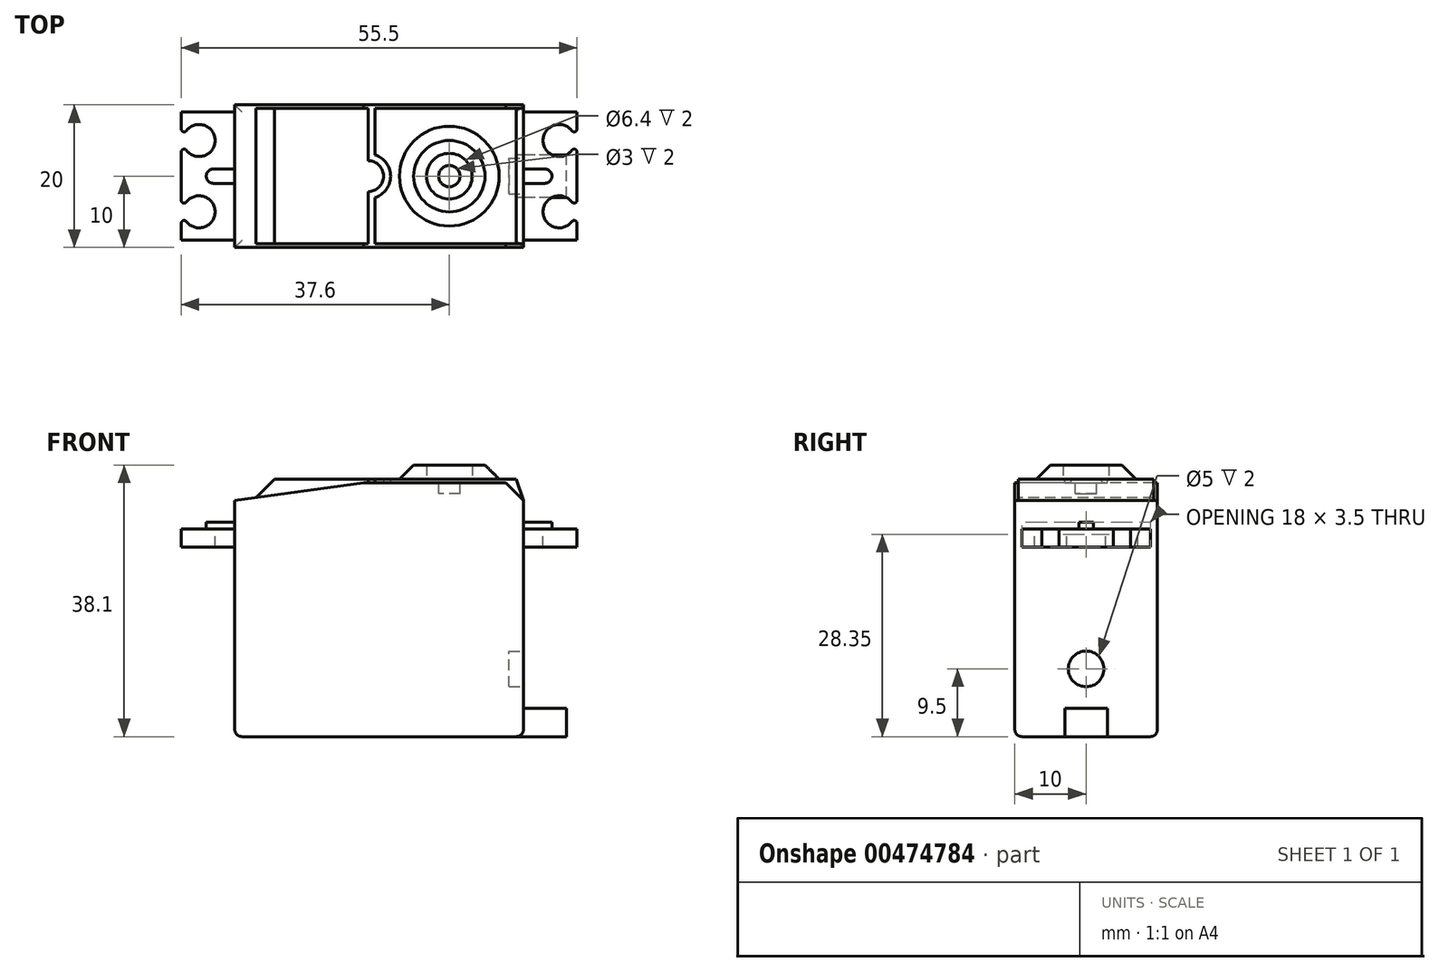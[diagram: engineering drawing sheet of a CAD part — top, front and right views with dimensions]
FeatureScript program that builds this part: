
annotation { "Feature Type Name" : "Feature", "Feature Type Description" : "" }
export const myFeature = defineFeature(function(context is Context, id is Id, definition is map)
    precondition{}
    {
        {
            var Q0;
            Q0=qCreatedBy(makeId("Front.planeOp"),FACE);
            var sketch = newSketch(context, id + "F0", { "sketchPlane" : qUnion([Q0])});
            skLineSegment(sketch, "E0.bottom", {"start": v(0, 0) * mm, "end": v(40.5, 0) * mm});
            skLineSegment(sketch, "E0.top", {"start": v(0, 36.1) * mm, "end": v(40.5, 36.1) * mm});
            skLineSegment(sketch, "E0.left", {"start": v(0, 0) * mm, "end": v(0, 26.6) * mm});
            skLineSegment(sketch, "E0.right", {"start": v(40.5, 0) * mm, "end": v(40.5, 26.6) * mm});
            skLineSegment(sketch, "E1", {"start": v(0, 29.1) * mm, "end": v(-7.5, 29.1) * mm});
            skLineSegment(sketch, "E2", {"start": v(-7.5, 29.1) * mm, "end": v(-7.5, 26.6) * mm});
            skLineSegment(sketch, "E3", {"start": v(-7.5, 26.6) * mm, "end": v(0, 26.6) * mm});
            skLineSegment(sketch, "E4", {"start": v(40.5, 29.1) * mm, "end": v(48, 29.1) * mm});
            skLineSegment(sketch, "E5", {"start": v(48, 29.1) * mm, "end": v(48, 26.6) * mm});
            skLineSegment(sketch, "E6", {"start": v(48, 26.6) * mm, "end": v(40.5, 26.6) * mm});
            skLineSegment(sketch, "E7.trimOffspring", {"start": v(0, 29.1) * mm, "end": v(0, 36.1) * mm});
            skLineSegment(sketch, "E8.trimOffspring", {"start": v(40.5, 29.1) * mm, "end": v(40.5, 36.1) * mm});
            skSolve(sketch);
        }
        {
            var Q0;
            Q0=qSketchRegion(id+"F0",true);
            extrude(context, id + "F1", {"entities" : qUnion([Q0]), "depth" : 20 * mm, "offsetDistance" : 25 * mm});
        }
        {
            var Q0;
            Q0=makeQuery(id+"F1.opExtrude","SWEPT_FACE",FACE,{"disambiguationData":[OSD([sQuery(id+"F0.wireOp",EDGE,"E1")])]});
            var sketch = newSketch(context, id + "F2", { "sketchPlane" : qUnion([Q0])});
            skLineSegment(sketch, "E9", {"start": v(0, -1) * mm, "end": v(-7.5, -1) * mm});
            skLineSegment(sketch, "E10", {"start": v(-7.5, -19) * mm, "end": v(0, -19) * mm});
            skLineSegment(sketch, "E11", {"start": v(0, -19) * mm, "end": v(0, -20) * mm});
            skLineSegment(sketch, "E12", {"start": v(0, -20) * mm, "end": v(-7.5, -20) * mm});
            skLineSegment(sketch, "E13", {"start": v(-7.5, 0) * mm, "end": v(0, 0) * mm});
            skArc(sketch, "E14", {"start": v(-6.8, -6.36) * mm, "mid": v(-2.75, -5) * mm, "end": v(-6.8, -3.64) * mm});
            skArc(sketch, "E15", {"start": v(-6.8, -16.36) * mm, "mid": v(-2.75, -15) * mm, "end": v(-6.8, -13.64) * mm});
            skLineSegment(sketch, "E16", {"start": v(-5, -5) * mm, "end": v(-5, -15) * mm, "construction": true});
            skLineSegment(sketch, "E17", {"start": v(-7.5, 0) * mm, "end": v(-7.5, -1) * mm});
            skLineSegment(sketch, "E18", {"start": v(-7.5, -19) * mm, "end": v(-7.5, -20) * mm});
            skLineSegment(sketch, "E19", {"start": v(20.25, 0) * mm, "end": v(20.25, -20) * mm, "construction": true});
            skArc(sketch, "E20", {"start": v(-7.5, -3.4) * mm, "mid": v(-7.23, -3.77) * mm, "end": v(-6.8, -3.64) * mm});
            skArc(sketch, "E21", {"start": v(-6.8, -6.36) * mm, "mid": v(-7.23, -6.23) * mm, "end": v(-7.5, -6.6) * mm});
            skLineSegment(sketch, "E22", {"start": v(-7.5, -5) * mm, "end": v(-5, -5) * mm, "construction": true});
            skLineSegment(sketch, "E23", {"start": v(-7.5, -3.4) * mm, "end": v(-7.5, -6.6) * mm});
            skLineSegment(sketch, "E24", {"start": v(-5, -15) * mm, "end": v(-7.5, -15) * mm, "construction": true});
            skArc(sketch, "E25", {"start": v(-7.5, -13.4) * mm, "mid": v(-7.23, -13.77) * mm, "end": v(-6.8, -13.64) * mm});
            skArc(sketch, "E26", {"start": v(-6.8, -16.36) * mm, "mid": v(-7.23, -16.23) * mm, "end": v(-7.5, -16.6) * mm});
            skLineSegment(sketch, "E27", {"start": v(-7.5, -13.4) * mm, "end": v(-7.5, -16.6) * mm});
            skArc(sketch, "E28.MirrorCS", {"start": v(48, -13.4) * mm, "mid": v(47.73, -13.77) * mm, "end": v(47.3, -13.64) * mm});
            skLineSegment(sketch, "E29.MirrorCS", {"start": v(40.5, -1) * mm, "end": v(48, -1) * mm});
            skLineSegment(sketch, "E30.MirrorCS", {"start": v(45.5, -15) * mm, "end": v(48, -15) * mm, "construction": true});
            skArc(sketch, "E31.MirrorCS", {"start": v(47.3, -6.36) * mm, "mid": v(47.73, -6.23) * mm, "end": v(48, -6.6) * mm});
            skLineSegment(sketch, "E32.MirrorCS", {"start": v(40.5, -20) * mm, "end": v(48, -20) * mm});
            skArc(sketch, "E33.MirrorCS", {"start": v(47.3, -16.36) * mm, "mid": v(47.73, -16.23) * mm, "end": v(48, -16.6) * mm});
            skArc(sketch, "E34.MirrorCS", {"start": v(48, -3.4) * mm, "mid": v(47.73, -3.77) * mm, "end": v(47.3, -3.64) * mm});
            skLineSegment(sketch, "E35.MirrorCS", {"start": v(48, -19) * mm, "end": v(48, -20) * mm});
            skLineSegment(sketch, "E36.MirrorCS", {"start": v(48, 0) * mm, "end": v(48, -1) * mm});
            skLineSegment(sketch, "E37.MirrorCS", {"start": v(48, -5) * mm, "end": v(45.5, -5) * mm, "construction": true});
            skLineSegment(sketch, "E38.MirrorCS", {"start": v(40.5, -19) * mm, "end": v(40.5, -20) * mm});
            skArc(sketch, "E39.MirrorCS", {"start": v(47.3, -6.36) * mm, "mid": v(43.25, -5) * mm, "end": v(47.3, -3.64) * mm});
            skArc(sketch, "E40.MirrorCS", {"start": v(47.3, -16.36) * mm, "mid": v(43.25, -15) * mm, "end": v(47.3, -13.64) * mm});
            skLineSegment(sketch, "E41.MirrorCS", {"start": v(48, -3.4) * mm, "end": v(48, -6.6) * mm});
            skLineSegment(sketch, "E42.MirrorCS", {"start": v(48, -13.4) * mm, "end": v(48, -16.6) * mm});
            skLineSegment(sketch, "E43.MirrorCS", {"start": v(48, 0) * mm, "end": v(40.5, 0) * mm});
            skLineSegment(sketch, "E44.MirrorCS", {"start": v(45.5, -5) * mm, "end": v(45.5, -15) * mm, "construction": true});
            skLineSegment(sketch, "E45.MirrorCS", {"start": v(48, -19) * mm, "end": v(40.5, -19) * mm});
            skLineSegment(sketch, "E46", {"start": v(0, -1) * mm, "end": v(0, 0) * mm});
            skLineSegment(sketch, "E47", {"start": v(40.5, 0) * mm, "end": v(40.5, -1) * mm});
            skSolve(sketch);
        }
        {
            var Q0;
            Q0=qSketchRegion(id+"F2",true);
            extrude(context, id + "F3", {"entities" : qUnion([Q0]), "operationType" : NewBodyOperationType.REMOVE, "endBound" : BoundingType.UP_TO_NEXT, "oppositeDirection" : true, "depth" : 25 * mm, "offsetDistance" : 25 * mm});
        }
        {
            var Q0;
            Q0=makeQuery(id+"F1.opExtrude","SWEPT_FACE",FACE,{"disambiguationData":[OSD([sQuery(id+"F0.wireOp",EDGE,"E1")])]});
            var sketch = newSketch(context, id + "F4", { "sketchPlane" : qUnion([Q0])});
            skLineSegment(sketch, "E48", {"start": v(0, -9) * mm, "end": v(0, -11) * mm});
            skLineSegment(sketch, "E49", {"start": v(0, -9) * mm, "end": v(-3, -9) * mm});
            skLineSegment(sketch, "E50", {"start": v(0, -11) * mm, "end": v(-3, -11) * mm});
            skArc(sketch, "E51", {"start": v(-3, -9) * mm, "mid": v(-4, -10) * mm, "end": v(-3, -11) * mm});
            skLineSegment(sketch, "E52", {"start": v(0, -10) * mm, "end": v(-3, -10) * mm, "construction": true});
            skLineSegment(sketch, "E53", {"start": v(20.25, 0) * mm, "end": v(20.25, -20) * mm, "construction": true});
            skLineSegment(sketch, "E54.MirrorCS", {"start": v(40.5, -9) * mm, "end": v(40.5, -11) * mm});
            skLineSegment(sketch, "E55.MirrorCS", {"start": v(40.5, -9) * mm, "end": v(43.5, -9) * mm});
            skLineSegment(sketch, "E56.MirrorCS", {"start": v(40.5, -11) * mm, "end": v(43.5, -11) * mm});
            skArc(sketch, "E57.MirrorCS", {"start": v(43.5, -9) * mm, "mid": v(44.5, -10) * mm, "end": v(43.5, -11) * mm});
            skLineSegment(sketch, "E58.MirrorCS", {"start": v(40.5, -10) * mm, "end": v(43.5, -10) * mm, "construction": true});
            skSolve(sketch);
        }
        {
            var Q0;
            Q0=qSketchRegion(id+"F4",true);
            extrude(context, id + "F5", {"entities" : qUnion([Q0]), "operationType" : NewBodyOperationType.ADD, "depth" : 1 * mm, "offsetDistance" : 25 * mm});
        }
        {
            var Q0;
            Q0=makeQuery(id+"F1.opExtrude","CAP_FACE",FACE,{"disambiguationData":[OSD([sQuery(id+"F0.wireOp",EDGE,"E0.bottom"),sQuery(id+"F0.wireOp",EDGE,"E0.top"),sQuery(id+"F0.wireOp",EDGE,"E0.left"),sQuery(id+"F0.wireOp",EDGE,"E0.right"),sQuery(id+"F0.wireOp",EDGE,"E1"),sQuery(id+"F0.wireOp",EDGE,"E2"),sQuery(id+"F0.wireOp",EDGE,"E3"),sQuery(id+"F0.wireOp",EDGE,"E4"),sQuery(id+"F0.wireOp",EDGE,"E5"),sQuery(id+"F0.wireOp",EDGE,"E6"),sQuery(id+"F0.wireOp",EDGE,"E7.trimOffspring"),sQuery(id+"F0.wireOp",EDGE,"E8.trimOffspring")])],"isStart":false});
            var sketch = newSketch(context, id + "F6", { "sketchPlane" : qUnion([Q0])});
            skLineSegment(sketch, "E59", {"start": v(0, 36.1) * mm, "end": v(40.5, 36.1) * mm});
            skLineSegment(sketch, "E60", {"start": v(40.5, 36.1) * mm, "end": v(40.5, 33.1) * mm});
            skLineSegment(sketch, "E61", {"start": v(40.5, 33.1) * mm, "end": v(38, 35.6) * mm});
            skLineSegment(sketch, "E62", {"start": v(38, 35.6) * mm, "end": v(18.1, 35.6) * mm});
            skLineSegment(sketch, "E63", {"start": v(18.1, 35.6) * mm, "end": v(0, 33.1) * mm});
            skLineSegment(sketch, "E64", {"start": v(0, 33.1) * mm, "end": v(0, 36.1) * mm});
            skLineSegment(sketch, "E65", {"start": v(30.1, 36.1) * mm, "end": v(30.1, 0) * mm, "construction": true});
            skSolve(sketch);
        }
        {
            var Q0;
            Q0=qSketchRegion(id+"F6",true);
            extrude(context, id + "F7", {"entities" : qUnion([Q0]), "operationType" : NewBodyOperationType.REMOVE, "endBound" : BoundingType.UP_TO_NEXT, "oppositeDirection" : true, "depth" : 25 * mm, "offsetDistance" : 25 * mm});
        }
        {
            var Q0;
            Q0=makeQuery(id+"F1.opExtrude","CAP_FACE",FACE,{"disambiguationData":[OSD([sQuery(id+"F0.wireOp",EDGE,"E0.bottom"),sQuery(id+"F0.wireOp",EDGE,"E0.top"),sQuery(id+"F0.wireOp",EDGE,"E0.left"),sQuery(id+"F0.wireOp",EDGE,"E0.right"),sQuery(id+"F0.wireOp",EDGE,"E1"),sQuery(id+"F0.wireOp",EDGE,"E2"),sQuery(id+"F0.wireOp",EDGE,"E3"),sQuery(id+"F0.wireOp",EDGE,"E4"),sQuery(id+"F0.wireOp",EDGE,"E5"),sQuery(id+"F0.wireOp",EDGE,"E6"),sQuery(id+"F0.wireOp",EDGE,"E7.trimOffspring"),sQuery(id+"F0.wireOp",EDGE,"E8.trimOffspring")])],"isStart":false});
            cPlane(context, id + "F8", {"entities" : qUnion([Q0]), "cplaneType" : CPlaneType.OFFSET, "offset" : 0.5 * mm, "oppositeDirection" : true, "width" : 150 * mm, "height" : 150 * mm});
        }
        {
            var Q0;
            Q0=qCreatedBy(id+"F8.planeOp",FACE);
            var sketch = newSketch(context, id + "F9", { "sketchPlane" : qUnion([Q0])});
            skLineSegment(sketch, "E66", {"start": v(3, 33.51) * mm, "end": v(5.59, 36.1) * mm});
            skLineSegment(sketch, "E67", {"start": v(5.59, 36.1) * mm, "end": v(18.7, 36.1) * mm});
            skLineSegment(sketch, "E68", {"start": v(18.7, 36.1) * mm, "end": v(18.7, 35.6) * mm});
            skLineSegment(sketch, "E69", {"start": v(18.7, 35.6) * mm, "end": v(18.1, 35.6) * mm});
            skLineSegment(sketch, "E70", {"start": v(18.1, 35.6) * mm, "end": v(3, 33.51) * mm});
            skLineSegment(sketch, "E71", {"start": v(19.7, 36.1) * mm, "end": v(39.5, 36.1) * mm});
            skLineSegment(sketch, "E72", {"start": v(39.5, 36.1) * mm, "end": v(40.5, 33.1) * mm});
            skLineSegment(sketch, "E73", {"start": v(40.5, 33.1) * mm, "end": v(38, 35.6) * mm});
            skLineSegment(sketch, "E74", {"start": v(38, 35.6) * mm, "end": v(19.7, 35.6) * mm});
            skLineSegment(sketch, "E75", {"start": v(19.7, 35.6) * mm, "end": v(19.7, 36.1) * mm});
            skLineSegment(sketch, "E76", {"start": v(30.1, 36.1) * mm, "end": v(30.1, 0) * mm, "construction": true});
            skSolve(sketch);
        }
        {
            var Q0;
            Q0=qSketchRegion(id+"F9",true);
            extrude(context, id + "F10", {"entities" : qUnion([Q0]), "operationType" : NewBodyOperationType.ADD, "oppositeDirection" : true, "depth" : 19 * mm, "offsetDistance" : 25 * mm});
        }
        {
            var Q0;
            Q0=makeQuery(id+"F10.opExtrude","SWEPT_FACE",FACE,{"disambiguationData":[OSD([sQuery(id+"F9.wireOp",EDGE,"E71")])]});
            var sketch = newSketch(context, id + "F11", { "sketchPlane" : qUnion([Q0])});
            skArc(sketch, "E77", {"start": v(19.7, -13) * mm, "mid": v(21.86, -10) * mm, "end": v(19.7, -7) * mm});
            skLineSegment(sketch, "E78", {"start": v(5.59, -10) * mm, "end": v(39.5, -10) * mm, "construction": true});
            skLineSegment(sketch, "E79", {"start": v(19.7, -7) * mm, "end": v(19.7, -13) * mm});
            skSolve(sketch);
        }
        {
            var Q0;
            Q0=qSketchRegion(id+"F11",true);
            var Q1;
            Q1=makeQuery(id+"F7.boolean.opBoolean","COPY",FACE,{"derivedFrom":makeQuery(id+"F7.opExtrude","SWEPT_FACE",FACE,{"disambiguationData":[OSD([sQuery(id+"F6.wireOp",EDGE,"E62")])]})});
            extrude(context, id + "F12", {"entities" : qUnion([Q0]), "operationType" : NewBodyOperationType.REMOVE, "endBound" : BoundingType.UP_TO_SURFACE, "oppositeDirection" : true, "depth" : 25 * mm, "endBoundEntityFace" : qUnion([Q1]), "offsetDistance" : 25 * mm});
        }
        {
            var Q0;
            {var subQ0=sQuery(id+"F6.wireOp",EDGE,"E62");Q0=makeQuery(id+"F12.boolean.opBoolean","MERGE",FACE,{"derivedFrom":[makeQuery(id+"F7.boolean.opBoolean","COPY",FACE,{"derivedFrom":makeQuery(id+"F7.opExtrude","SWEPT_FACE",FACE,{"disambiguationData":[OSD([subQ0])]})}),makeQuery(id+"F12.opExtrude","CAP_FACE",FACE,{"disambiguationData":[OSD([subQ0])],"isStart":false})]});}
            var sketch = newSketch(context, id + "F13", { "sketchPlane" : qUnion([Q0])});
            skArc(sketch, "E80", {"start": v(18.7, -12.16) * mm, "mid": v(20.86, -10) * mm, "end": v(18.7, -7.84) * mm});
            skLineSegment(sketch, "E81", {"start": v(18.7, -7.84) * mm, "end": v(18.7, -12.16) * mm});
            skSolve(sketch);
        }
        {
            var Q0;
            Q0=qSketchRegion(id+"F13",true);
            extrude(context, id + "F14", {"entities" : qUnion([Q0]), "operationType" : NewBodyOperationType.ADD, "depth" : 0.5 * mm, "offsetDistance" : 25 * mm});
        }
        {
            var Q0;
            Q0=makeQuery(id+"F10.opExtrude","SWEPT_FACE",FACE,{"disambiguationData":[OSD([sQuery(id+"F9.wireOp",EDGE,"E71")])]});
            var sketch = newSketch(context, id + "F15", { "sketchPlane" : qUnion([Q0])});
            skCircle(sketch, "E82", {"center": v(30.1, -10) * mm, "radius": 7 * mm});
            skLineSegment(sketch, "E83", {"start": v(21.86, -10) * mm, "end": v(39.5, -10) * mm, "construction": true});
            skCircle(sketch, "E84", {"center": v(30.1, -10) * mm, "radius": 3.2 * mm});
            skSolve(sketch);
        }
        {
            var Q0;
            Q0=qSketchRegion(id+"F15",true);
            extrude(context, id + "F16", {"entities" : qUnion([Q0]), "operationType" : NewBodyOperationType.ADD, "depth" : 2 * mm, "offsetDistance" : 25 * mm});
        }
        {
            var Q0;
            Q0=makeQuery(id+"F16.opExtrude","CAP_EDGE",EDGE,{"disambiguationData":[OSD([sQuery(id+"F15.wireOp",EDGE,"E82")])],"isStart":false});
            chamfer(context, id + "F17", {"entities" : qUnion([Q0]), "width" : 2 * mm, "tangentPropagation" : true});
        }
        {
            var Q0;
            Q0=makeQuery(id+"F16.boolean.opBoolean","SPLIT",FACE,{"disambiguationData":[TD([makeQuery(id+"F16.opExtrude","SWEPT_FACE",FACE,{"disambiguationData":[OSD([sQuery(id+"F15.wireOp",EDGE,"E84")])]})])],"derivedFrom":makeQuery(id+"F10.opExtrude","SWEPT_FACE",FACE,{"disambiguationData":[OSD([sQuery(id+"F9.wireOp",EDGE,"E71")])]})});
            var sketch = newSketch(context, id + "F18", { "sketchPlane" : qUnion([Q0])});
            skCircle(sketch, "E85", {"center": v(30.1, -10) * mm, "radius": 1.5 * mm});
            skSolve(sketch);
        }
        {
            var Q0;
            Q0=qSketchRegion(id+"F18",true);
            extrude(context, id + "F19", {"entities" : qUnion([Q0]), "operationType" : NewBodyOperationType.REMOVE, "oppositeDirection" : true, "depth" : 2 * mm, "offsetDistance" : 25 * mm});
        }
        {
            var Q0;
            Q0=makeQuery(id+"F24.opFillet","SPLIT",FACE,{"disambiguationData":[OD(0.0)],"derivedFrom":makeQuery(id+"F3.boolean.opBoolean","MERGE",FACE,{"derivedFrom":[makeQuery(id+"F1.opExtrude","SWEPT_FACE",FACE,{"disambiguationData":[OSD([sQuery(id+"F0.wireOp",EDGE,"E0.right")])]}),makeQuery(id+"F1.opExtrude","SWEPT_FACE",FACE,{"disambiguationData":[OSD([sQuery(id+"F0.wireOp",EDGE,"E8.trimOffspring")])]}),makeQuery(id+"F3.opExtrude","SWEPT_FACE",FACE,{"disambiguationData":[OSD([sQuery(id+"F2.wireOp",EDGE,"E38.MirrorCS")])]}),makeQuery(id+"F3.opExtrude","SWEPT_FACE",FACE,{"disambiguationData":[OSD([sQuery(id+"F2.wireOp",EDGE,"E47")])]})]})});
            var sketch = newSketch(context, id + "F20", { "sketchPlane" : qUnion([Q0])});
            skCircle(sketch, "E86", {"center": v(-10, 9.5) * mm, "radius": 2.5 * mm});
            skLineSegment(sketch, "E87", {"start": v(-10, 26.6) * mm, "end": v(-10, 0) * mm, "construction": true});
            skSolve(sketch);
        }
        {
            var Q0;
            Q0=qSketchRegion(id+"F20",true);
            extrude(context, id + "F21", {"entities" : qUnion([Q0]), "operationType" : NewBodyOperationType.REMOVE, "oppositeDirection" : true, "depth" : 2 * mm, "offsetDistance" : 25 * mm});
        }
        {
            var Q0;
            Q0=makeQuery(id+"F3.boolean.opBoolean","MERGE",FACE,{"derivedFrom":[makeQuery(id+"F1.opExtrude","SWEPT_FACE",FACE,{"disambiguationData":[OSD([sQuery(id+"F0.wireOp",EDGE,"E0.right")])]}),makeQuery(id+"F1.opExtrude","SWEPT_FACE",FACE,{"disambiguationData":[OSD([sQuery(id+"F0.wireOp",EDGE,"E8.trimOffspring")])]}),makeQuery(id+"F3.opExtrude","SWEPT_FACE",FACE,{"disambiguationData":[OSD([sQuery(id+"F2.wireOp",EDGE,"E38.MirrorCS")])]}),makeQuery(id+"F3.opExtrude","SWEPT_FACE",FACE,{"disambiguationData":[OSD([sQuery(id+"F2.wireOp",EDGE,"E47")])]})]});
            var sketch = newSketch(context, id + "F22", { "sketchPlane" : qUnion([Q0])});
            skLineSegment(sketch, "E88.bottom", {"start": v(-13, 4) * mm, "end": v(-7, 4) * mm});
            skLineSegment(sketch, "E88.top", {"start": v(-13, 0) * mm, "end": v(-7, 0) * mm});
            skLineSegment(sketch, "E88.left", {"start": v(-13, 4) * mm, "end": v(-13, 0) * mm});
            skLineSegment(sketch, "E88.right", {"start": v(-7, 4) * mm, "end": v(-7, 0) * mm});
            skLineSegment(sketch, "E89", {"start": v(-10, 26.6) * mm, "end": v(-10, 0) * mm, "construction": true});
            skSolve(sketch);
        }
        {
            var Q0;
            Q0=qSketchRegion(id+"F22",true);
            extrude(context, id + "F23", {"entities" : qUnion([Q0]), "operationType" : NewBodyOperationType.ADD, "depth" : 6 * mm, "offsetDistance" : 25 * mm});
        }
        {
            var Q0;
            {var subQ0=sQuery(id+"F0.wireOp",EDGE,"E7.trimOffspring");Q0=makeQuery(id+"F3.boolean.opBoolean","MERGE",EDGE,{"derivedFrom":[makeQuery(id+"F1.opExtrude","CAP_EDGE",EDGE,{"disambiguationData":[OSD([sQuery(id+"F0.wireOp",EDGE,"E0.left")])],"isStart":true}),makeQuery(id+"F1.opExtrude","CAP_EDGE",EDGE,{"disambiguationData":[OSD([subQ0])],"isStart":true}),makeQuery(id+"F3.opExtrude","SWEPT_EDGE",EDGE,{"disambiguationData":[OSD([sQuery(id+"F0.wireOp",EDGE,"E1"),subQ0,sQuery(id+"F2.wireOp",EDGE,"E13"),sQuery(id+"F2.wireOp",EDGE,"E46")])]})]});}
            var Q1;
            {var subQ0=sQuery(id+"F0.wireOp",EDGE,"E7.trimOffspring");Q1=makeQuery(id+"F3.boolean.opBoolean","MERGE",EDGE,{"derivedFrom":[makeQuery(id+"F1.opExtrude","CAP_EDGE",EDGE,{"disambiguationData":[OSD([sQuery(id+"F0.wireOp",EDGE,"E0.left")])],"isStart":false}),makeQuery(id+"F1.opExtrude","CAP_EDGE",EDGE,{"disambiguationData":[OSD([subQ0])],"isStart":false}),makeQuery(id+"F3.opExtrude","SWEPT_EDGE",EDGE,{"disambiguationData":[OSD([sQuery(id+"F0.wireOp",EDGE,"E1"),subQ0,sQuery(id+"F2.wireOp",EDGE,"E11"),sQuery(id+"F2.wireOp",EDGE,"E12")])]})]});}
            var Q2;
            {var subQ0=sQuery(id+"F0.wireOp",EDGE,"E0.right");Q2=makeQuery(id+"F3.boolean.opBoolean","MERGE",EDGE,{"derivedFrom":[makeQuery(id+"F1.opExtrude","CAP_EDGE",EDGE,{"disambiguationData":[OSD([subQ0])],"isStart":false}),makeQuery(id+"F1.opExtrude","CAP_EDGE",EDGE,{"disambiguationData":[OSD([sQuery(id+"F0.wireOp",EDGE,"E8.trimOffspring")])],"isStart":false}),makeQuery(id+"F3.opExtrude","SWEPT_EDGE",EDGE,{"disambiguationData":[OSD([subQ0,sQuery(id+"F0.wireOp",EDGE,"E6")])]})]});}
            var Q3;
            {var subQ0=sQuery(id+"F0.wireOp",EDGE,"E6");var subQ1=sQuery(id+"F0.wireOp",EDGE,"E0.right");Q3=makeQuery(id+"F3.boolean.opBoolean","MERGE",EDGE,{"derivedFrom":[makeQuery(id+"F1.opExtrude","CAP_EDGE",EDGE,{"disambiguationData":[OSD([subQ1])],"isStart":true}),makeQuery(id+"F1.opExtrude","CAP_EDGE",EDGE,{"disambiguationData":[OSD([sQuery(id+"F0.wireOp",EDGE,"E8.trimOffspring")])],"isStart":true}),makeQuery(id+"F3.opExtrude","SWEPT_EDGE",EDGE,{"disambiguationData":[OSD([subQ1,subQ0]),TDD([makeQuery(id+"F1.opExtrude","CAP_VERTEX",VERTEX,{"disambiguationData":[OSD([subQ1,subQ0])],"isStart":true})])]})]});}
            var Q4;
            Q4=makeQuery(id+"F3.boolean.opBoolean","COPY",EDGE,{"derivedFrom":makeQuery(id+"F3.opExtrude","SWEPT_EDGE",EDGE,{"disambiguationData":[OSD([sQuery(id+"F0.wireOp",EDGE,"E1"),sQuery(id+"F0.wireOp",EDGE,"E2"),sQuery(id+"F2.wireOp",EDGE,"E10"),sQuery(id+"F2.wireOp",EDGE,"E18")])]})});
            var Q5;
            Q5=makeQuery(id+"F3.boolean.opBoolean","COPY",EDGE,{"derivedFrom":makeQuery(id+"F3.opExtrude","SWEPT_EDGE",EDGE,{"disambiguationData":[OSD([sQuery(id+"F0.wireOp",EDGE,"E1"),sQuery(id+"F0.wireOp",EDGE,"E2"),sQuery(id+"F2.wireOp",EDGE,"E9"),sQuery(id+"F2.wireOp",EDGE,"E17")])]})});
            var Q6;
            Q6=makeQuery(id+"F3.boolean.opBoolean","COPY",EDGE,{"derivedFrom":makeQuery(id+"F3.opExtrude","SWEPT_EDGE",EDGE,{"disambiguationData":[OSD([sQuery(id+"F2.wireOp",EDGE,"E29.MirrorCS"),sQuery(id+"F2.wireOp",EDGE,"E36.MirrorCS")])]})});
            var Q7;
            Q7=makeQuery(id+"F3.boolean.opBoolean","COPY",EDGE,{"derivedFrom":makeQuery(id+"F3.opExtrude","SWEPT_EDGE",EDGE,{"disambiguationData":[OSD([sQuery(id+"F2.wireOp",EDGE,"E35.MirrorCS"),sQuery(id+"F2.wireOp",EDGE,"E45.MirrorCS")])]})});
            var Q8;
            Q8=makeQuery(id+"F1.opExtrude","CAP_EDGE",EDGE,{"disambiguationData":[OSD([sQuery(id+"F0.wireOp",EDGE,"E0.bottom")])],"isStart":false});
            var Q9;
            Q9=makeQuery(id+"F1.opExtrude","SWEPT_EDGE",EDGE,{"disambiguationData":[OSD([sQuery(id+"F0.wireOp",EDGE,"E0.bottom"),sQuery(id+"F0.wireOp",EDGE,"E0.left")])]});
            var Q10;
            Q10=makeQuery(id+"F1.opExtrude","CAP_EDGE",EDGE,{"disambiguationData":[OSD([sQuery(id+"F0.wireOp",EDGE,"E0.bottom")])],"isStart":true});
            var Q11;
            Q11=makeQuery(id+"F1.opExtrude","SWEPT_EDGE",EDGE,{"disambiguationData":[OSD([sQuery(id+"F0.wireOp",EDGE,"E0.bottom"),sQuery(id+"F0.wireOp",EDGE,"E0.right")])]});
            fillet(context, id + "F24", {"entities" : qUnion([Q0, Q1, Q2, Q3, Q4, Q5, Q6, Q7, Q8, Q9, Q10, Q11]), "radius" : 1 * mm, "tangentPropagation" : true, "allowEdgeOverflow" : false});
        }
    });
